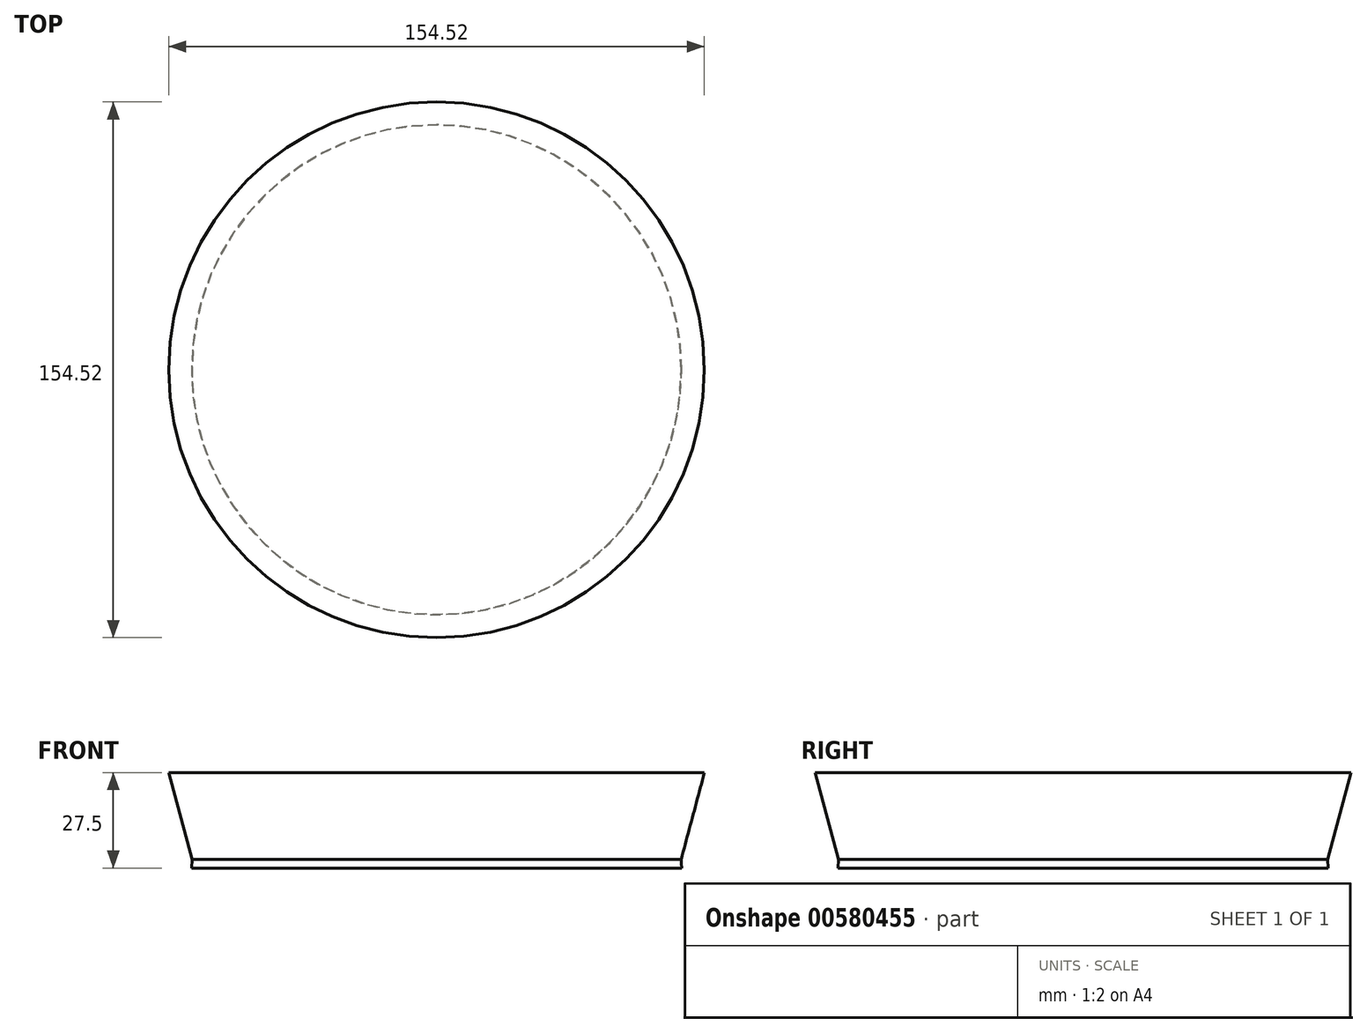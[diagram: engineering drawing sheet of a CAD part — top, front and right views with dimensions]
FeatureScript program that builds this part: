
annotation { "Feature Type Name" : "Feature", "Feature Type Description" : "" }
export const myFeature = defineFeature(function(context is Context, id is Id, definition is map)
    precondition{}
    {
        {
            var Q0;
            Q0=qCreatedBy(makeId("Top.planeOp"),FACE);
            var sketch = newSketch(context, id + "F0", { "sketchPlane" : qUnion([Q0])});
            skCircle(sketch, "E0", {"center": v(0, 0) * mm, "radius": 70.56 * mm});
            skSolve(sketch);
        }
        {
            var Q0;
            Q0=makeQuery(id+"F0.imprint","IMPRINT",FACE,{"disambiguationData":[TD([[makeQuery(id+"F0.imprint","IMPRINT",EDGE,{"derivedFrom":sQuery(id+"F0.wireOp",EDGE,"E0")}),1.0]])]});
            extrude(context, id + "F1", {"entities" : qUnion([Q0]), "depth" : 25 * mm, "offsetDistance" : 25 * mm, "hasDraft" : true, "draftAngle" : 15 * degree, "hasSecondDirection" : true, "secondDirectionOppositeDirection" : true, "secondDirectionDepth" : 2.5 * mm, "hasSecondDirectionDraft" : true, "secondDirectionDraftAngle" : 3 * degree});
        }
    });
